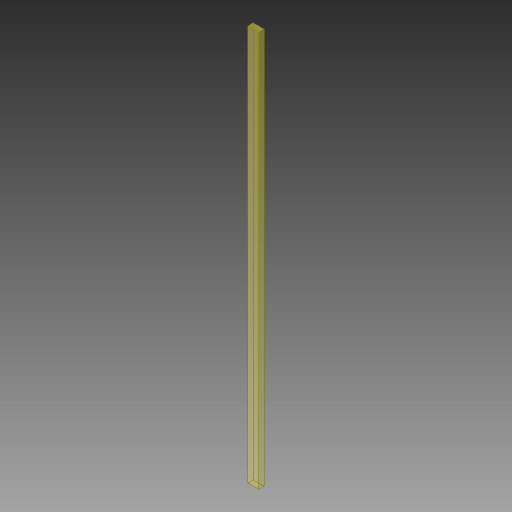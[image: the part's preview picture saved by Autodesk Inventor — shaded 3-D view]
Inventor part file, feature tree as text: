
AUTODESK INVENTOR PART (.ipt)
format: ipt  version: 2018.1 (Build 221171000, 171)  size: 89,088 bytes
history: native  units: mm
features: other x1, extrude x1, sketch x1
ambient origin geometry x8: Origin, YZ Plane, XZ Plane, XY Plane, X Axis, Y Axis, Z Axis, Center Point
bodies: Solid1 (feature_tree)
feature tree (3):
  parser-record x1  (decoder bookkeeping rows leaked as tree rows — omitted from the tree; the rows remain in map.json)
  extrude  "Extrusion1"  Depth=370.0mm
  sketch  "Sketch1"  dims[d0=10.0mm d1=370.0mm d2=5.0mm d3=0.0mm]
note: 1 file-system path scrubbed to <path> (originals preserved in map.json)
